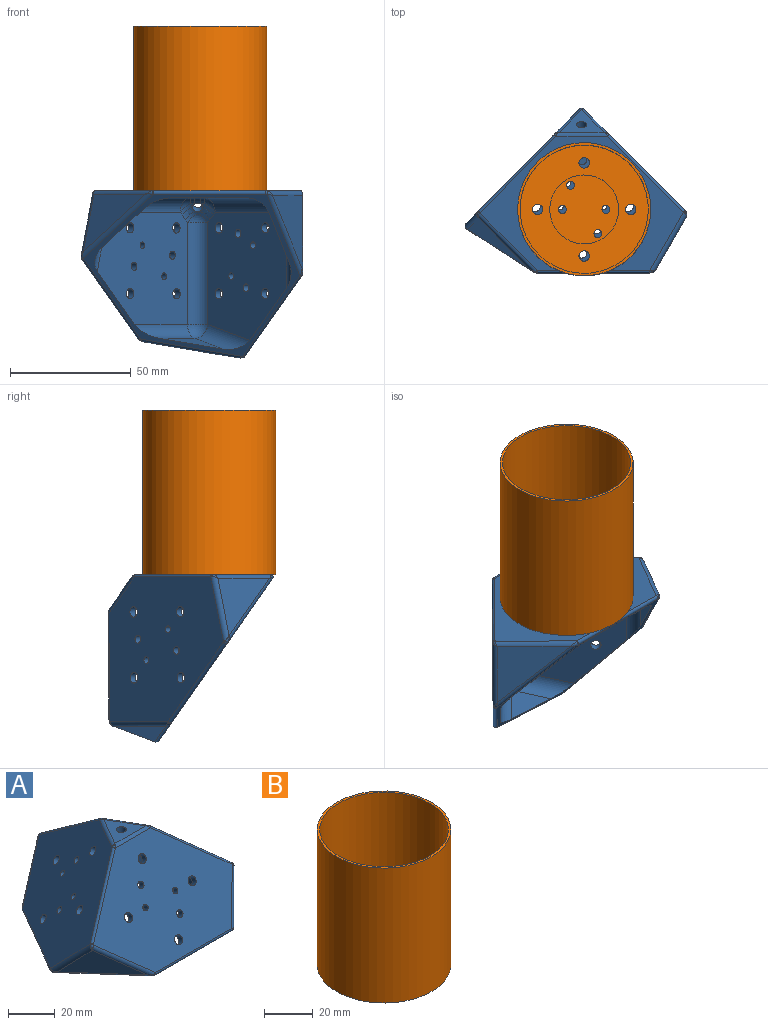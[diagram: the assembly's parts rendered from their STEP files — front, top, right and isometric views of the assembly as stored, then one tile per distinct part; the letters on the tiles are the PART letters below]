
ASSEMBLY  parts=2 mates=1
PART A: 105 faces, bbox 93.4x91x54.7 mm
  f0: plane 1.64x1.42mm, normal (0,0,-1), area 1mm2, adj f56,f89,f94
  f1: plane 1.64x1.42mm, normal (0,0,-1), area 1mm2, adj f56,f98,f99
  f2: plane 84.17x45.57mm, normal (0,-0.82,0.57), area 3148.6mm2, adj f17,f19,f20,f24,f33,f39,f53,f73
  f3: plane 72.83x45.57mm, normal (0.71,0.41,0.57), area 3148.6mm2, adj f17,f18,f28,f34,f36,f40,f43,f65
  f4: plane 72.96x47.02mm, normal (-0.71,0.41,0.57), area 3148.6mm2, adj f18,f19,f23,f25,f29,f30,f48,f57
  f5: plane 65.44x42.46mm, normal (0,0.82,-0.57), area 2033.8mm2, adj f8,f73,f74,f75,f76,f77,f78,f79
  f6: plane 56.67x42.46mm, normal (-0.71,-0.41,-0.57), area 2033.8mm2, adj f8,f65,f66,f67,f68,f69,f70,f71
  f7: plane 56.67x42.46mm, normal (0.71,-0.41,-0.57), area 2033.8mm2, adj f8,f57,f58,f59,f60,f61,f62,f63
  f8: plane 90.14x82.61mm, normal (0,0,-1), area 546.2mm2, adj f5,f6,f7,f13,f14,f15,f21,f26
  f9: plane 28.96x25.78mm, normal (-0.68,-0.61,-0.41), area 370.5mm2, adj f20,f21,f23
  f10: plane 36.8x17.44mm, normal (0.87,-0.29,-0.41), area 370.5mm2, adj f36,f37,f39
  f11: plane 37.97x17.44mm, normal (-0.18,0.89,-0.41), area 370.5mm2, adj f25,f26,f28
  f12: plane 18.53x16.05mm, normal (0,0,1), area 134.1mm2, adj f30,f33,f34,f56
  f13: plane 19.93x17.74mm, normal (0.68,0.61,0.41), area 175.5mm2, adj f8,f100,f101
  f14: plane 25.33x12mm, normal (-0.87,0.29,0.41), area 175.5mm2, adj f8,f81,f82
  f15: plane 26.13x12mm, normal (0.18,-0.89,0.41), area 175.5mm2, adj f8,f83,f84
  f16: plane 1.64x1.42mm, normal (0,0,-1), area 1mm2, adj f56,f90,f95
  f17: cylinder r=1mm len=32.03mm, axis (0.7,-0.41,-0.58), area 70.1mm2, adj f2,f3,f35,f40
  f18: cylinder r=1mm len=36.34mm, axis (0,0.81,-0.58), area 70.1mm2, adj f3,f4,f29,f32
  f19: cylinder r=1mm len=32.03mm, axis (-0.7,-0.41,-0.58), area 70.1mm2, adj f2,f4,f24,f31
  f20: cylinder r=2mm len=25.33mm, axis (0.71,-0.4,-0.58), area 84.1mm2, adj f2,f9,f22,f51,f52
  f21: cylinder r=2mm len=33.5mm, axis (-0.66,0.75,0), area 94.2mm2, adj f8,f9,f50,f51
  f22: bspline ~3.13x1.48mm, area 2.4mm2, adj f20,f23,f24
  f23: cylinder r=2mm len=21.72mm, axis (0.18,-0.68,0.71), area 83mm2, adj f4,f9,f22,f24,f49,f50
  f24: bspline ~1.53x1.21mm, area 0.7mm2, adj f2,f19,f22,f23
  f25: cylinder r=2mm len=24.9mm, axis (-0.7,-0.41,-0.58), area 84.1mm2, adj f4,f11,f27,f46,f47
  f26: cylinder r=2mm len=42.71mm, axis (0.98,0.2,0), area 94.2mm2, adj f8,f11,f45,f46
  f27: bspline ~3.13x1.42mm, area 2.4mm2, adj f25,f28,f29
  f28: cylinder r=2mm len=21.72mm, axis (-0.68,0.18,0.71), area 83mm2, adj f3,f11,f27,f29,f44,f45
  f29: bspline ~1.47x1.15mm, area 0.7mm2, adj f4,f18,f27,f28
  f30: cylinder r=2mm len=19.32mm, axis (0.5,0.87,0), area 38.3mm2, adj f4,f12,f31,f32
  f31: bspline ~2.27x1.7mm, area 1.2mm2, adj f19,f30,f33
  f32: bspline ~2.62x1.47mm, area 1.2mm2, adj f18,f30,f34
  f33: cylinder r=2mm len=21.37mm, axis (-1,0,0), area 38.3mm2, adj f2,f12,f31,f35
  f34: cylinder r=2mm len=19.32mm, axis (0.5,-0.87,0), area 38.3mm2, adj f3,f12,f32,f35
  f35: bspline ~2.27x1.7mm, area 1.2mm2, adj f17,f33,f34
  f36: cylinder r=2mm len=29mm, axis (0,0.82,-0.58), area 84.1mm2, adj f3,f10,f38,f41,f42
  f37: cylinder r=2mm len=41.61mm, axis (-0.31,-0.95,0), area 94.2mm2, adj f8,f10,f41,f55
  f38: bspline ~3.13x1.36mm, area 2.4mm2, adj f36,f39,f40
  f39: cylinder r=2mm len=21.72mm, axis (0.5,0.5,0.71), area 83mm2, adj f2,f10,f38,f40,f54,f55
  f40: bspline ~1.44x1.39mm, area 0.7mm2, adj f3,f17,f38,f39
  f41: bspline ~3.38x1.48mm, area 3.4mm2, adj f36,f37,f42
  f42: bspline ~1.77x1.66mm, area 0.7mm2, adj f8,f36,f41,f43
  f43: cylinder r=1mm len=40.58mm, axis (-0.5,0.87,0), area 101mm2, adj f3,f8,f42,f44
  f44: bspline ~2.39x1.72mm, area 1.7mm2, adj f8,f28,f43,f45
  f45: bspline ~2.85x1.45mm, area 2.9mm2, adj f26,f28,f44
  f46: bspline ~3.7x2.44mm, area 3.4mm2, adj f25,f26,f47
  f47: bspline ~2.17x1.65mm, area 0.7mm2, adj f8,f25,f46,f48
  f48: cylinder r=1mm len=40.58mm, axis (-0.5,-0.87,0), area 101mm2, adj f4,f8,f47,f49
  f49: bspline ~1.95x1.77mm, area 1.7mm2, adj f8,f23,f48,f50
  f50: bspline ~3.08x1.52mm, area 2.9mm2, adj f21,f23,f49
  f51: bspline ~3.06x1.68mm, area 3.4mm2, adj f20,f21,f52
  f52: bspline ~2.09x1.65mm, area 0.7mm2, adj f8,f20,f51,f53
  f53: cylinder r=1mm len=46.28mm, axis (1,0,0), area 101mm2, adj f2,f8,f52,f54
  f54: bspline ~2.2x1.62mm, area 1.7mm2, adj f8,f39,f53,f55
  f55: bspline ~2.73x2.47mm, area 2.9mm2, adj f37,f39,f54
  f56: cylinder r=2.15mm len=4.3mm, axis (0,0,1), area 40.5mm2, adj f0,f1,f12,f16,f86,f96,f97
  f57: cylinder r=1.65mm len=4.45mm, axis (-0.71,0.41,0.57), area 31.1mm2, adj f4,f7
  f58: cylinder r=2.15mm len=5.24mm, axis (-0.71,0.41,0.57), area 40.5mm2, adj f4,f7
  f59: cylinder r=1.4mm len=4.1mm, axis (-0.71,0.41,0.57), area 26.4mm2, adj f4,f7
  f60: cylinder r=1.65mm len=4.45mm, axis (-0.71,0.41,0.57), area 31.1mm2, adj f4,f7
  f61: cylinder r=2.15mm len=5.24mm, axis (-0.71,0.41,0.57), area 40.5mm2, adj f4,f7
  f62: cylinder r=1.4mm len=4.1mm, axis (-0.71,0.41,0.57), area 26.4mm2, adj f4,f7
  f63: cylinder r=2.15mm len=5.24mm, axis (-0.71,0.41,0.57), area 40.5mm2, adj f4,f7
  f64: cylinder r=2.15mm len=5.24mm, axis (-0.71,0.41,0.57), area 40.5mm2, adj f4,f7
  f65: cylinder r=2.15mm len=5.24mm, axis (0.71,0.41,0.57), area 40.5mm2, adj f3,f6
  f66: cylinder r=2.15mm len=5.24mm, axis (0.71,0.41,0.57), area 40.5mm2, adj f3,f6
  f67: cylinder r=1.4mm len=4.1mm, axis (0.71,0.41,0.57), area 26.4mm2, adj f3,f6
  f68: cylinder r=2.15mm len=5.24mm, axis (0.71,0.41,0.57), area 40.5mm2, adj f3,f6
  f69: cylinder r=2.15mm len=5.24mm, axis (0.71,0.41,0.57), area 40.5mm2, adj f3,f6
  f70: cylinder r=1.4mm len=4.1mm, axis (0.71,0.41,0.57), area 26.4mm2, adj f3,f6
  f71: cylinder r=1.65mm len=4.45mm, axis (0.71,0.41,0.57), area 31.1mm2, adj f3,f6
  f72: cylinder r=1.65mm len=4.45mm, axis (0.71,0.41,0.57), area 31.1mm2, adj f3,f6
  f73: cylinder r=2.15mm len=5.24mm, axis (0,-0.82,0.57), area 40.5mm2, adj f2,f5
  f74: cylinder r=2.15mm len=5.24mm, axis (0,-0.82,0.57), area 40.5mm2, adj f2,f5
  f75: cylinder r=1.4mm len=4.06mm, axis (0,-0.82,0.57), area 26.4mm2, adj f2,f5
  f76: cylinder r=2.15mm len=5.24mm, axis (0,-0.82,0.57), area 40.5mm2, adj f2,f5
  f77: cylinder r=1.65mm len=4.42mm, axis (0,-0.82,0.57), area 31.1mm2, adj f2,f5
  f78: cylinder r=1.4mm len=4.06mm, axis (0,-0.82,0.57), area 26.4mm2, adj f2,f5
  f79: cylinder r=2.15mm len=5.24mm, axis (0,-0.82,0.57), area 40.5mm2, adj f2,f5
  f80: cylinder r=1.65mm len=4.42mm, axis (0,-0.82,0.57), area 31.1mm2, adj f2,f5
  f81: cylinder r=6mm len=23.8mm, axis (-0.5,-0.5,-0.71), area 198.6mm2, adj f5,f8,f14,f85
  f82: cylinder r=6mm len=29.43mm, axis (0,-0.82,0.58), area 202.5mm2, adj f6,f8,f14,f85
  f83: cylinder r=6mm len=23.8mm, axis (0.68,-0.18,-0.71), area 198.6mm2, adj f6,f8,f15,f87
  f84: cylinder r=6mm len=24.96mm, axis (0.7,0.41,0.58), area 202.5mm2, adj f7,f8,f15,f87
  f85: sphere r=6mm, area 48.8mm2, adj f81,f82,f88
  f86: bspline ~5.57x4.73mm, area 14.3mm2, adj f6,f56,f89,f90
  f87: sphere r=6mm, area 49.5mm2, adj f83,f84,f91
  f88: cylinder r=6mm len=34.02mm, axis (-0.7,0.41,0.58), area 399.7mm2, adj f5,f6,f85,f92
  f89: cylinder r=6mm len=5.08mm, axis (-0.5,0.87,0), area 9.5mm2, adj f0,f6,f86,f92
  f90: cylinder r=6mm len=5.08mm, axis (-0.5,0.87,0), area 9.5mm2, adj f6,f16,f86,f93
  f91: cylinder r=6mm len=35.4mm, axis (0,-0.81,0.58), area 399.7mm2, adj f6,f7,f87,f93
  f92: sphere r=6mm, area 19.1mm2, adj f88,f89,f94
  f93: sphere r=6mm, area 19.1mm2, adj f90,f91,f95
  f94: cylinder r=6mm len=4.92mm, axis (1,0,0), area 9.5mm2, adj f0,f5,f92,f96
  f95: cylinder r=6mm len=5.08mm, axis (-0.5,-0.87,0), area 9.5mm2, adj f7,f16,f93,f97
  f96: bspline ~4.92x2.62mm, area 14.3mm2, adj f5,f56,f94,f98
  f97: bspline ~6.11x5.45mm, area 14.3mm2, adj f7,f56,f95,f99
  f98: cylinder r=6mm len=4.92mm, axis (1,0,0), area 9.5mm2, adj f1,f5,f96,f102
  f99: cylinder r=6mm len=5.08mm, axis (-0.5,-0.87,0), area 9.5mm2, adj f1,f7,f97,f102
  f100: cylinder r=6mm len=23.8mm, axis (-0.18,0.68,-0.71), area 198.6mm2, adj f7,f8,f13,f103
  f101: cylinder r=6mm len=26.01mm, axis (-0.71,0.4,0.58), area 202.5mm2, adj f5,f8,f13,f103
  f102: sphere r=6mm, area 19.1mm2, adj f98,f99,f104
  f103: sphere r=6mm, area 49.5mm2, adj f100,f101,f104
  f104: cylinder r=6mm len=34.02mm, axis (0.7,0.41,0.58), area 399.7mm2, adj f5,f7,f102,f103
PART B: 15 faces, bbox 55x55x68 mm
  f0: cylinder r=26.5mm len=63mm, axis (0,0,-1), area 10489.8mm2, adj f2,f14
  f1: cylinder r=27.5mm len=68mm, axis (0,0,-1), area 11749.6mm2, adj f2,f12
  f2: plane 55x55mm, normal (0,0,1), area 169.6mm2, adj f0,f1
  f3: plane 28.5x28.5mm, normal (0,0,1), area 603.7mm2, adj f4,f5,f6,f11,f13
  f4: cylinder r=1.65mm len=3.3mm, axis (0,0,1), area 31.1mm2, adj f3,f12
  f5: cylinder r=1.65mm len=3.3mm, axis (0,0,1), area 31.1mm2, adj f3,f12
  f6: cylinder r=1.65mm len=3.3mm, axis (0,0,1), area 31.1mm2, adj f3,f12
  f7: cylinder r=2.15mm len=5mm, axis (0,0,1), area 67.5mm2, adj f12,f14
  f8: cylinder r=2.15mm len=5mm, axis (0,0,1), area 67.5mm2, adj f12,f14
  f9: cylinder r=2.15mm len=5mm, axis (0,0,1), area 67.5mm2, adj f12,f14
  f10: cylinder r=2.15mm len=5mm, axis (0,0,1), area 67.5mm2, adj f12,f14
  f11: cylinder r=1.65mm len=3.3mm, axis (0,0,1), area 31.1mm2, adj f3,f12
  f12: plane 55x55mm, normal (0,0,-1), area 2283.5mm2, adj f1,f4,f5,f6,f7,f8,f9,f10
  f13: cylinder r=14.25mm len=28.5mm, axis (0,0,-1), area 179.1mm2, adj f3,f14
  f14: plane 53x53mm, normal (0,0,1), area 1510.2mm2, adj f0,f7,f8,f9,f10,f13
PLACE A rot(axis=(-1,0,0),55deg) t=(-29.62,-59.63,-79.01)mm
PLACE B t=(-28.58,-55.35,-43.25)mm
MATE parallel A.f2 <-> B.f1  axis (0,0,1) through (-28.56,-55.39,-46.25)mm
